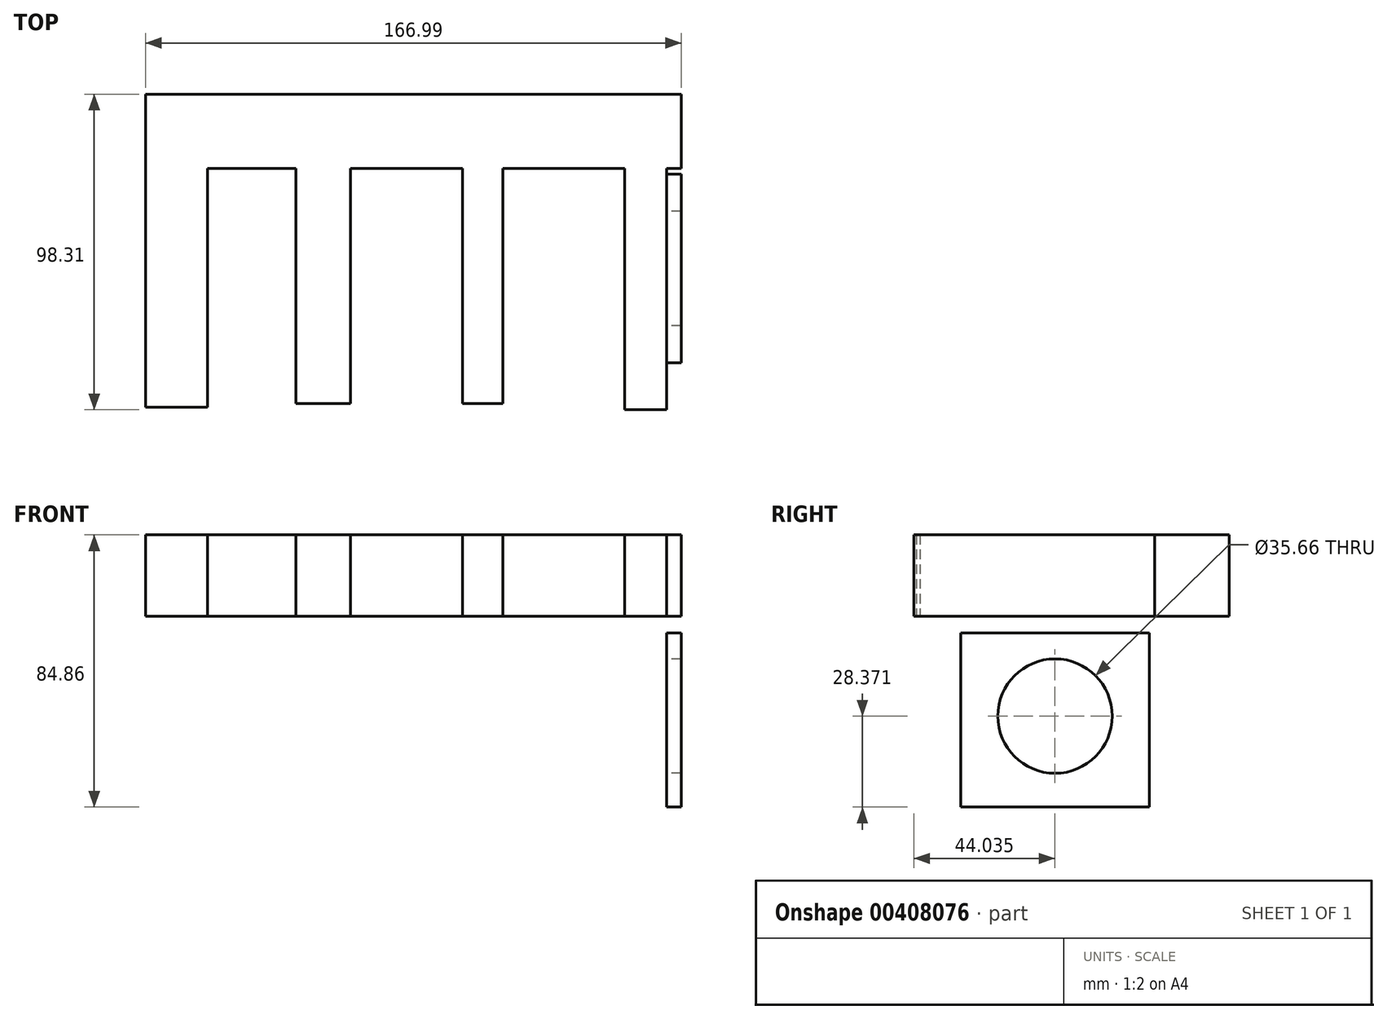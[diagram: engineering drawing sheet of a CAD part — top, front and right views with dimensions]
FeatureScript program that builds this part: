
annotation { "Feature Type Name" : "Feature", "Feature Type Description" : "" }
export const myFeature = defineFeature(function(context is Context, id is Id, definition is map)
    precondition{}
    {
        {
            var Q0;
            Q0=qCreatedBy(makeId("Top.planeOp"),FACE);
            var sketch = newSketch(context, id + "F0", { "sketchPlane" : qUnion([Q0])});
            skLineSegment(sketch, "E0.bottom", {"start": v(-86.49, 44.86) * mm, "end": v(80.5, 44.86) * mm});
            skLineSegment(sketch, "E0.top", {"start": v(-86.49, 21.7) * mm, "end": v(80.5, 21.7) * mm});
            skLineSegment(sketch, "E0.left", {"start": v(-86.49, 44.86) * mm, "end": v(-86.49, 21.7) * mm});
            skLineSegment(sketch, "E0.right", {"start": v(80.5, 44.86) * mm, "end": v(80.5, 21.7) * mm});
            skLineSegment(sketch, "E1.bottom", {"start": v(-86.49, 21.7) * mm, "end": v(-67.21, 21.7) * mm});
            skLineSegment(sketch, "E1.top", {"start": v(-86.49, -52.64) * mm, "end": v(-67.21, -52.64) * mm});
            skLineSegment(sketch, "E1.left", {"start": v(-86.49, 21.7) * mm, "end": v(-86.49, -52.64) * mm});
            skLineSegment(sketch, "E1.right", {"start": v(-67.21, 21.7) * mm, "end": v(-67.21, -52.64) * mm});
            skLineSegment(sketch, "E2.bottom", {"start": v(-39.68, 21.7) * mm, "end": v(-22.67, 21.7) * mm});
            skLineSegment(sketch, "E2.top", {"start": v(-39.68, -51.5) * mm, "end": v(-22.67, -51.5) * mm});
            skLineSegment(sketch, "E2.left", {"start": v(-39.68, 21.7) * mm, "end": v(-39.68, -51.5) * mm});
            skLineSegment(sketch, "E2.right", {"start": v(-22.67, 21.7) * mm, "end": v(-22.67, -51.5) * mm});
            skLineSegment(sketch, "E3.bottom", {"start": v(12.3, 21.7) * mm, "end": v(24.94, 21.7) * mm});
            skLineSegment(sketch, "E3.top", {"start": v(12.3, -51.5) * mm, "end": v(24.94, -51.5) * mm});
            skLineSegment(sketch, "E3.left", {"start": v(12.3, 21.7) * mm, "end": v(12.3, -51.5) * mm});
            skLineSegment(sketch, "E3.right", {"start": v(24.94, 21.7) * mm, "end": v(24.94, -51.5) * mm});
            skLineSegment(sketch, "E4.bottom", {"start": v(62.84, 21.7) * mm, "end": v(75.96, 21.7) * mm});
            skLineSegment(sketch, "E4.top", {"start": v(62.84, -53.45) * mm, "end": v(75.96, -53.45) * mm});
            skLineSegment(sketch, "E4.left", {"start": v(62.84, 21.7) * mm, "end": v(62.84, -53.45) * mm});
            skLineSegment(sketch, "E4.right", {"start": v(75.96, 21.7) * mm, "end": v(75.96, -53.45) * mm});
            skSolve(sketch);
        }
        {
            var Q0;
            Q0=qCreatedBy(makeId("Right.planeOp"),FACE);
            var sketch = newSketch(context, id + "F1", { "sketchPlane" : qUnion([Q0])});
            skLineSegment(sketch, "E5.bottom", {"start": v(-38.82, -17.87) * mm, "end": v(19.99, -17.87) * mm});
            skLineSegment(sketch, "E5.top", {"start": v(-38.82, -72.16) * mm, "end": v(19.99, -72.16) * mm});
            skLineSegment(sketch, "E5.left", {"start": v(-38.82, -17.87) * mm, "end": v(-38.82, -72.16) * mm});
            skLineSegment(sketch, "E5.right", {"start": v(19.99, -17.87) * mm, "end": v(19.99, -72.16) * mm});
            skCircle(sketch, "E6", {"center": v(-9.42, -43.79) * mm, "radius": 17.83 * mm});
            skPoint(sketch, "E6.centerSnap0", {"position": v(-9.42, -72.16) * mm});
            skSolve(sketch);
        }
        {
            var Q0;
            Q0 = qSketchRegion(id + "F0", true);
            extrude(context, id + "F2", {"entities" : qUnion([Q0]), "endBound" : BoundingType.SYMMETRIC, "depth" : 25.4 * mm});
        }
        {
            var Q0;
            Q0=makeQuery(id+"F1.imprint","IMPRINT",FACE,{"disambiguationData":[TD([[makeQuery(id+"F1.imprint","IMPRINT",EDGE,{"derivedFrom":sQuery(id+"F1.wireOp",EDGE,"E5.bottom")}),-1.0]])]});
            var Q1;
            Q1=makeQuery(id+"F2.opExtrude","SWEPT_FACE",FACE,{"disambiguationData":[OSD([sQuery(id+"F0.wireOp",EDGE,"E0.right")])]});
            var Q2;
            Q2=makeQuery(id+"F2.opExtrude","CAP_VERTEX",VERTEX,{"disambiguationData":[OSD([sQuery(id+"F0.wireOp",EDGE,"E0.top"),sQuery(id+"F0.wireOp",EDGE,"E0.right")])],"isStart":true});
            var Q3;
            Q3=makeQuery(id+"F2.opExtrude","SWEPT_FACE",FACE,{"disambiguationData":[OSD([sQuery(id+"F0.wireOp",EDGE,"E4.right")])]});
            var Q4;
            Q4=makeQuery(id+"F2.opExtrude","CAP_VERTEX",VERTEX,{"disambiguationData":[OSD([sQuery(id+"F0.wireOp",EDGE,"E0.top"),sQuery(id+"F0.wireOp",EDGE,"E4.bottom"),sQuery(id+"F0.wireOp",EDGE,"E4.right")])],"isStart":true});
            extrude(context, id + "F3", {"entities" : qUnion([Q0]), "endBound" : BoundingType.UP_TO_VERTEX, "endBoundEntityFace" : qUnion([Q1]), "endBoundEntityVertex" : qUnion([Q2]), "depth" : 80.62 * mm, "hasSecondDirection" : true, "secondDirectionBound" : SecondDirectionBoundingType.UP_TO_VERTEX, "secondDirectionOppositeDirection" : false, "secondDirectionBoundEntityFace" : qUnion([Q3]), "secondDirectionBoundEntityVertex" : qUnion([Q4]), "secondDirectionDepth" : 75.95 * mm});
        }
        {
            var Q0;
            {var subQ0=sQuery(id+"F0.wireOp",EDGE,"E0.top");Q0=makeQuery(id+"F2.opExtrude","SWEPT_FACE",FACE,{"disambiguationData":[OSD([subQ0]),TDD([makeQuery(id+"F0.imprint","IMPRINT",EDGE,{"disambiguationData":[TD([[makeQuery(id+"F0.imprint","INTERSECT",VERTEX,{"derivedFrom":[subQ0,sQuery(id+"F0.wireOp",EDGE,"E3.bottom"),sQuery(id+"F0.wireOp",EDGE,"E3.right")]}),-1.0]])],"derivedFrom":subQ0})])]});}
            cPlane(context, id + "F4", {"entities" : qUnion([Q0]), "cplaneType" : CPlaneType.OFFSET, "offset" : 38.6 * mm, "width" : 152.4 * mm, "height" : 152.4 * mm});
        }
    });
